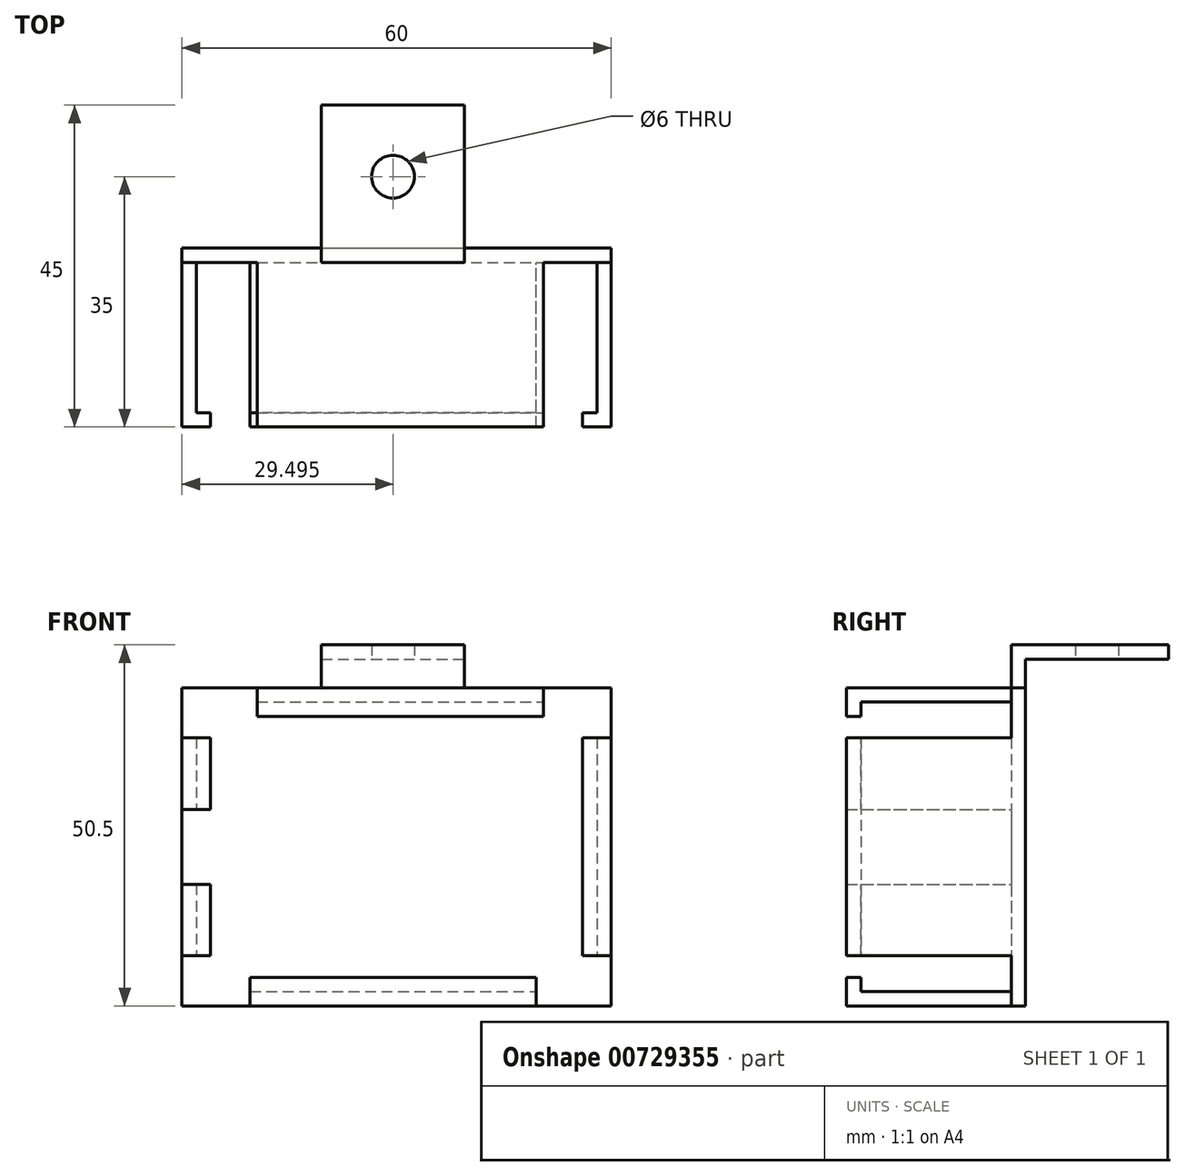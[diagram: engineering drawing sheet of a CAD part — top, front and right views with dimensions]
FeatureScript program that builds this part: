
annotation { "Feature Type Name" : "Feature", "Feature Type Description" : "" }
export const myFeature = defineFeature(function(context is Context, id is Id, definition is map)
    precondition{}
    {
        {
            var Q0;
            Q0=qCreatedBy(makeId("Front.planeOp"),FACE);
            var sketch = newSketch(context, id + "F0", { "sketchPlane" : qUnion([Q0])});
            skLineSegment(sketch, "E0.bottom", {"start": v(-39.22, 21.16) * mm, "end": v(20.78, 21.16) * mm});
            skLineSegment(sketch, "E0.top", {"start": v(-39.22, -23.34) * mm, "end": v(20.78, -23.34) * mm});
            skLineSegment(sketch, "E0.left", {"start": v(-39.22, 21.16) * mm, "end": v(-39.22, -23.34) * mm});
            skLineSegment(sketch, "E0.right", {"start": v(20.78, 21.16) * mm, "end": v(20.78, -23.34) * mm});
            skSolve(sketch);
        }
        {
            var Q0;
            Q0 = qSketchRegion(id + "F0", true);
            extrude(context, id + "F1", {"entities" : qUnion([Q0]), "depth" : 2 * mm, "offsetDistance" : 25 * mm});
        }
        {
            var Q0;
            Q0=makeQuery(id+"F1.opExtrude","CAP_FACE",FACE,{"disambiguationData":[OSD([sQuery(id+"F0.wireOp",EDGE,"E0.bottom"),sQuery(id+"F0.wireOp",EDGE,"E0.top"),sQuery(id+"F0.wireOp",EDGE,"E0.left"),sQuery(id+"F0.wireOp",EDGE,"E0.right")])],"isStart":false});
            var sketch = newSketch(context, id + "F2", { "sketchPlane" : qUnion([Q0])});
            skLineSegment(sketch, "E1.bottom", {"start": v(-28.72, 21.16) * mm, "end": v(11.28, 21.16) * mm});
            skLineSegment(sketch, "E1.top", {"start": v(-28.72, 19.16) * mm, "end": v(11.28, 19.16) * mm});
            skLineSegment(sketch, "E1.left", {"start": v(-28.72, 21.16) * mm, "end": v(-28.72, 19.16) * mm});
            skLineSegment(sketch, "E1.right", {"start": v(11.28, 21.16) * mm, "end": v(11.28, 19.16) * mm});
            skLineSegment(sketch, "E2.bottom", {"start": v(-29.72, -23.34) * mm, "end": v(10.28, -23.34) * mm});
            skLineSegment(sketch, "E2.top", {"start": v(-29.72, -21.34) * mm, "end": v(10.28, -21.34) * mm});
            skLineSegment(sketch, "E2.left", {"start": v(-29.72, -23.34) * mm, "end": v(-29.72, -21.34) * mm});
            skLineSegment(sketch, "E2.right", {"start": v(10.28, -23.34) * mm, "end": v(10.28, -21.34) * mm});
            skLineSegment(sketch, "E3.bottom", {"start": v(18.78, 14.16) * mm, "end": v(20.78, 14.16) * mm});
            skLineSegment(sketch, "E3.top", {"start": v(18.78, -16.34) * mm, "end": v(20.78, -16.34) * mm});
            skLineSegment(sketch, "E3.left", {"start": v(18.78, 14.16) * mm, "end": v(18.78, -16.34) * mm});
            skLineSegment(sketch, "E3.right", {"start": v(20.78, 14.16) * mm, "end": v(20.78, -16.34) * mm});
            skLineSegment(sketch, "E4.bottom", {"start": v(-39.22, 14.16) * mm, "end": v(-37.22, 14.16) * mm});
            skLineSegment(sketch, "E4.top", {"start": v(-39.22, 4.16) * mm, "end": v(-37.22, 4.16) * mm});
            skLineSegment(sketch, "E4.left", {"start": v(-39.22, 14.16) * mm, "end": v(-39.22, 4.16) * mm});
            skLineSegment(sketch, "E4.right", {"start": v(-37.22, 14.16) * mm, "end": v(-37.22, 4.16) * mm});
            skLineSegment(sketch, "E5.bottom", {"start": v(-39.22, -6.34) * mm, "end": v(-37.22, -6.34) * mm});
            skLineSegment(sketch, "E5.top", {"start": v(-39.22, -16.34) * mm, "end": v(-37.22, -16.34) * mm});
            skLineSegment(sketch, "E5.left", {"start": v(-39.22, -6.34) * mm, "end": v(-39.22, -16.34) * mm});
            skLineSegment(sketch, "E5.right", {"start": v(-37.22, -6.34) * mm, "end": v(-37.22, -16.34) * mm});
            skSolve(sketch);
        }
        {
            var Q0;
            Q0 = qSketchRegion(id + "F2", true);
            extrude(context, id + "F3", {"entities" : qUnion([Q0]), "operationType" : NewBodyOperationType.ADD, "depth" : 23 * mm, "offsetDistance" : 25 * mm});
        }
        {
            var Q0;
            Q0=makeQuery(id+"F3.boolean.opBoolean","MERGE",FACE,{"derivedFrom":[makeQuery(id+"F1.opExtrude","SWEPT_FACE",FACE,{"disambiguationData":[OSD([sQuery(id+"F0.wireOp",EDGE,"E0.top")])]}),makeQuery(id+"F3.opExtrude","SWEPT_FACE",FACE,{"disambiguationData":[OSD([sQuery(id+"F2.wireOp",EDGE,"E2.bottom")])]})]});
            var sketch = newSketch(context, id + "F4", { "sketchPlane" : qUnion([Q0])});
            skLineSegment(sketch, "E6.bottom", {"start": v(-29.72, 25) * mm, "end": v(10.28, 25) * mm});
            skLineSegment(sketch, "E6.top", {"start": v(-29.72, 23) * mm, "end": v(10.28, 23) * mm});
            skLineSegment(sketch, "E6.left", {"start": v(-29.72, 25) * mm, "end": v(-29.72, 23) * mm});
            skLineSegment(sketch, "E6.right", {"start": v(10.28, 25) * mm, "end": v(10.28, 23) * mm});
            skSolve(sketch);
        }
        {
            var Q0;
            Q0 = qSketchRegion(id + "F4", true);
            extrude(context, id + "F5", {"entities" : qUnion([Q0]), "operationType" : NewBodyOperationType.ADD, "oppositeDirection" : true, "depth" : 4 * mm, "offsetDistance" : 25 * mm});
        }
        {
            var Q0;
            Q0=makeQuery(id+"F3.boolean.opBoolean","MERGE",FACE,{"derivedFrom":[makeQuery(id+"F1.opExtrude","SWEPT_FACE",FACE,{"disambiguationData":[OSD([sQuery(id+"F0.wireOp",EDGE,"E0.left")])]}),makeQuery(id+"F3.opExtrude","SWEPT_FACE",FACE,{"disambiguationData":[OSD([sQuery(id+"F2.wireOp",EDGE,"E4.left")])]}),makeQuery(id+"F3.opExtrude","SWEPT_FACE",FACE,{"disambiguationData":[OSD([sQuery(id+"F2.wireOp",EDGE,"E5.left")])]})]});
            var sketch = newSketch(context, id + "F6", { "sketchPlane" : qUnion([Q0])});
            skLineSegment(sketch, "E7.bottom", {"start": v(25, 14.16) * mm, "end": v(23, 14.16) * mm});
            skLineSegment(sketch, "E7.top", {"start": v(25, 4.16) * mm, "end": v(23, 4.16) * mm});
            skLineSegment(sketch, "E7.left", {"start": v(25, 14.16) * mm, "end": v(25, 4.16) * mm});
            skLineSegment(sketch, "E7.right", {"start": v(23, 14.16) * mm, "end": v(23, 4.16) * mm});
            skLineSegment(sketch, "E8.bottom", {"start": v(25, -6.34) * mm, "end": v(23, -6.34) * mm});
            skLineSegment(sketch, "E8.top", {"start": v(25, -16.34) * mm, "end": v(23, -16.34) * mm});
            skLineSegment(sketch, "E8.left", {"start": v(25, -6.34) * mm, "end": v(25, -16.34) * mm});
            skLineSegment(sketch, "E8.right", {"start": v(23, -6.34) * mm, "end": v(23, -16.34) * mm});
            skSolve(sketch);
        }
        {
            var Q0;
            Q0 = qSketchRegion(id + "F6", true);
            extrude(context, id + "F7", {"entities" : qUnion([Q0]), "operationType" : NewBodyOperationType.ADD, "oppositeDirection" : true, "depth" : 4 * mm, "offsetDistance" : 25 * mm});
        }
        {
            var Q0;
            Q0=makeQuery(id+"F3.boolean.opBoolean","MERGE",FACE,{"derivedFrom":[makeQuery(id+"F1.opExtrude","SWEPT_FACE",FACE,{"disambiguationData":[OSD([sQuery(id+"F0.wireOp",EDGE,"E0.bottom")])]}),makeQuery(id+"F3.opExtrude","SWEPT_FACE",FACE,{"disambiguationData":[OSD([sQuery(id+"F2.wireOp",EDGE,"E1.bottom")])]})]});
            var sketch = newSketch(context, id + "F8", { "sketchPlane" : qUnion([Q0])});
            skLineSegment(sketch, "E9.bottom", {"start": v(-28.72, -25) * mm, "end": v(11.28, -25) * mm});
            skLineSegment(sketch, "E9.top", {"start": v(-28.72, -23) * mm, "end": v(11.28, -23) * mm});
            skLineSegment(sketch, "E9.left", {"start": v(-28.72, -25) * mm, "end": v(-28.72, -23) * mm});
            skLineSegment(sketch, "E9.right", {"start": v(11.28, -25) * mm, "end": v(11.28, -23) * mm});
            skSolve(sketch);
        }
        {
            var Q0;
            Q0 = qSketchRegion(id + "F8", true);
            extrude(context, id + "F9", {"entities" : qUnion([Q0]), "operationType" : NewBodyOperationType.ADD, "oppositeDirection" : true, "depth" : 4 * mm, "offsetDistance" : 25 * mm});
        }
        {
            var Q0;
            Q0=makeQuery(id+"F3.boolean.opBoolean","MERGE",FACE,{"derivedFrom":[makeQuery(id+"F1.opExtrude","SWEPT_FACE",FACE,{"disambiguationData":[OSD([sQuery(id+"F0.wireOp",EDGE,"E0.right")])]}),makeQuery(id+"F3.opExtrude","SWEPT_FACE",FACE,{"disambiguationData":[OSD([sQuery(id+"F2.wireOp",EDGE,"E3.right")])]})]});
            var sketch = newSketch(context, id + "F10", { "sketchPlane" : qUnion([Q0])});
            skLineSegment(sketch, "E10.bottom", {"start": v(-25, 14.16) * mm, "end": v(-23, 14.16) * mm});
            skLineSegment(sketch, "E10.top", {"start": v(-25, -16.34) * mm, "end": v(-23, -16.34) * mm});
            skLineSegment(sketch, "E10.left", {"start": v(-25, 14.16) * mm, "end": v(-25, -16.34) * mm});
            skLineSegment(sketch, "E10.right", {"start": v(-23, 14.16) * mm, "end": v(-23, -16.34) * mm});
            skSolve(sketch);
        }
        {
            var Q0;
            Q0 = qSketchRegion(id + "F10", true);
            extrude(context, id + "F11", {"entities" : qUnion([Q0]), "operationType" : NewBodyOperationType.ADD, "oppositeDirection" : true, "depth" : 4 * mm, "offsetDistance" : 25 * mm});
        }
        {
            var Q0;
            Q0=makeQuery(id+"F3.boolean.opBoolean","MERGE",FACE,{"derivedFrom":[makeQuery(id+"F1.opExtrude","SWEPT_FACE",FACE,{"disambiguationData":[OSD([sQuery(id+"F0.wireOp",EDGE,"E0.bottom")])]}),makeQuery(id+"F3.opExtrude","SWEPT_FACE",FACE,{"disambiguationData":[OSD([sQuery(id+"F2.wireOp",EDGE,"E1.bottom")])]})]});
            var sketch = newSketch(context, id + "F12", { "sketchPlane" : qUnion([Q0])});
            skLineSegment(sketch, "E11.bottom", {"start": v(-19.72, 0) * mm, "end": v(0.28, 0) * mm});
            skLineSegment(sketch, "E11.top", {"start": v(-19.72, -2) * mm, "end": v(0.28, -2) * mm});
            skLineSegment(sketch, "E11.left", {"start": v(-19.72, 0) * mm, "end": v(-19.72, -2) * mm});
            skLineSegment(sketch, "E11.right", {"start": v(0.28, 0) * mm, "end": v(0.28, -2) * mm});
            skSolve(sketch);
        }
        {
            var Q0;
            Q0 = qSketchRegion(id + "F12", true);
            extrude(context, id + "F13", {"entities" : qUnion([Q0]), "operationType" : NewBodyOperationType.ADD, "depth" : 6 * mm, "offsetDistance" : 25 * mm});
        }
        {
            var Q0;
            Q0=makeQuery(id+"F13.opExtrude","SWEPT_FACE",FACE,{"disambiguationData":[OSD([sQuery(id+"F12.wireOp",EDGE,"E11.top")])]});
            var sketch = newSketch(context, id + "F14", { "sketchPlane" : qUnion([Q0])});
            skLineSegment(sketch, "E12.bottom", {"start": v(-19.72, 27.16) * mm, "end": v(0.28, 27.16) * mm});
            skLineSegment(sketch, "E12.top", {"start": v(-19.72, 25.16) * mm, "end": v(0.28, 25.16) * mm});
            skLineSegment(sketch, "E12.left", {"start": v(-19.72, 27.16) * mm, "end": v(-19.72, 25.16) * mm});
            skLineSegment(sketch, "E12.right", {"start": v(0.28, 27.16) * mm, "end": v(0.28, 25.16) * mm});
            skSolve(sketch);
        }
        {
            var Q0;
            Q0 = qSketchRegion(id + "F14", true);
            extrude(context, id + "F15", {"entities" : qUnion([Q0]), "operationType" : NewBodyOperationType.ADD, "oppositeDirection" : true, "depth" : 22 * mm, "offsetDistance" : 25 * mm});
        }
        {
            var Q0;
            Q0=makeQuery(id+"F15.opExtrude","SWEPT_FACE",FACE,{"disambiguationData":[OSD([sQuery(id+"F14.wireOp",EDGE,"E12.top")])]});
            var sketch = newSketch(context, id + "F16", { "sketchPlane" : qUnion([Q0])});
            skCircle(sketch, "E13", {"center": v(-9.72, -10) * mm, "radius": 3 * mm});
            skPoint(sketch, "E13.centerSnap0", {"position": v(-9.72, -20) * mm});
            skPoint(sketch, "E13.centerSnap1", {"position": v(0.28, -10) * mm});
            skSolve(sketch);
        }
        {
            var Q0;
            Q0 = qSketchRegion(id + "F16", true);
            extrude(context, id + "F17", {"entities" : qUnion([Q0]), "operationType" : NewBodyOperationType.REMOVE, "oppositeDirection" : true, "depth" : 3 * mm, "offsetDistance" : 25 * mm});
        }
    });
